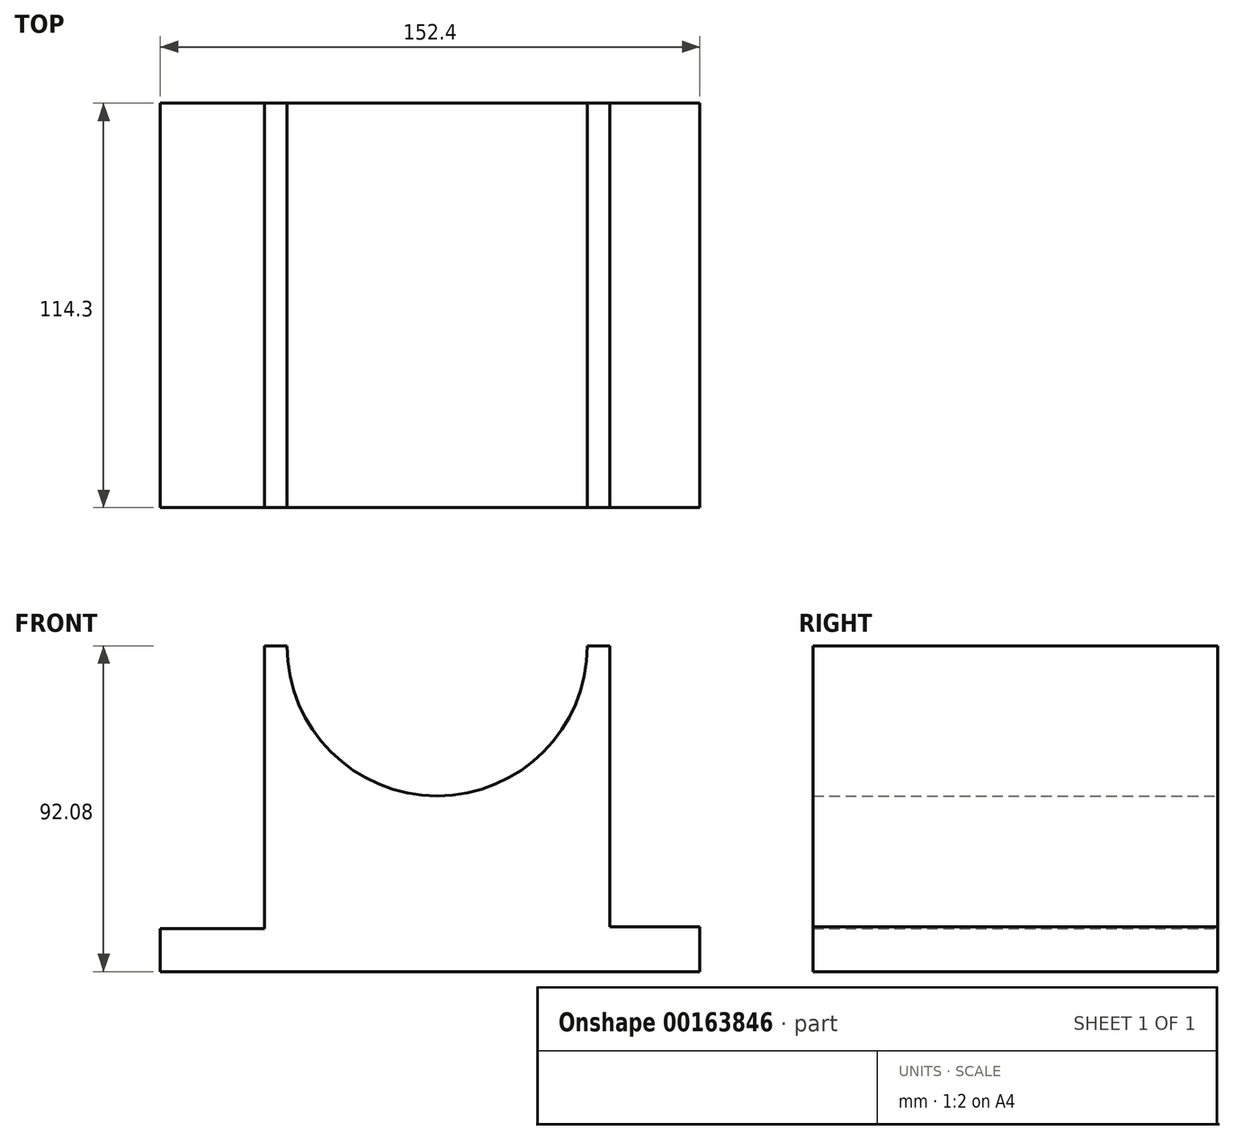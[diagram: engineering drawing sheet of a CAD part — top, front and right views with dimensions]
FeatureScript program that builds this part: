
annotation { "Feature Type Name" : "Feature", "Feature Type Description" : "" }
export const myFeature = defineFeature(function(context is Context, id is Id, definition is map)
    precondition{}
    {
        {
            var Q0;
            Q0=qCreatedBy(makeId("Front.planeOp"),FACE);
            var sketch = newSketch(context, id + "F0", { "sketchPlane" : qUnion([Q0])});
            skLineSegment(sketch, "E0", {"start": v(0, 0) * mm, "end": v(152.4, 0) * mm});
            skLineSegment(sketch, "E1", {"start": v(152.4, 0) * mm, "end": v(152.4, 12.7) * mm});
            skLineSegment(sketch, "E2", {"start": v(152.4, 12.7) * mm, "end": v(127, 12.7) * mm});
            skLineSegment(sketch, "E3", {"start": v(0, 0) * mm, "end": v(0, 12.09) * mm});
            skLineSegment(sketch, "E4", {"start": v(0, 12.09) * mm, "end": v(29.43, 12.09) * mm});
            skLineSegment(sketch, "E5", {"start": v(29.43, 12.09) * mm, "end": v(29.43, 92.08) * mm});
            skLineSegment(sketch, "E6", {"start": v(29.43, 92.08) * mm, "end": v(35.78, 92.08) * mm});
            skLineSegment(sketch, "E7", {"start": v(127, 92.08) * mm, "end": v(127, 12.7) * mm});
            skArc(sketch, "E8", {"start": v(35.78, 92.08) * mm, "mid": v(78.21, 49.64) * mm, "end": v(120.65, 92.08) * mm});
            skLineSegment(sketch, "E9.trimOffspring", {"start": v(120.65, 92.08) * mm, "end": v(127, 92.08) * mm});
            skSolve(sketch);
        }
        {
            var Q0;
            Q0 = qSketchRegion(id + "F0", true);
            extrude(context, id + "F1", {"entities" : qUnion([Q0]), "depth" : 114.3 * mm});
        }
    });
